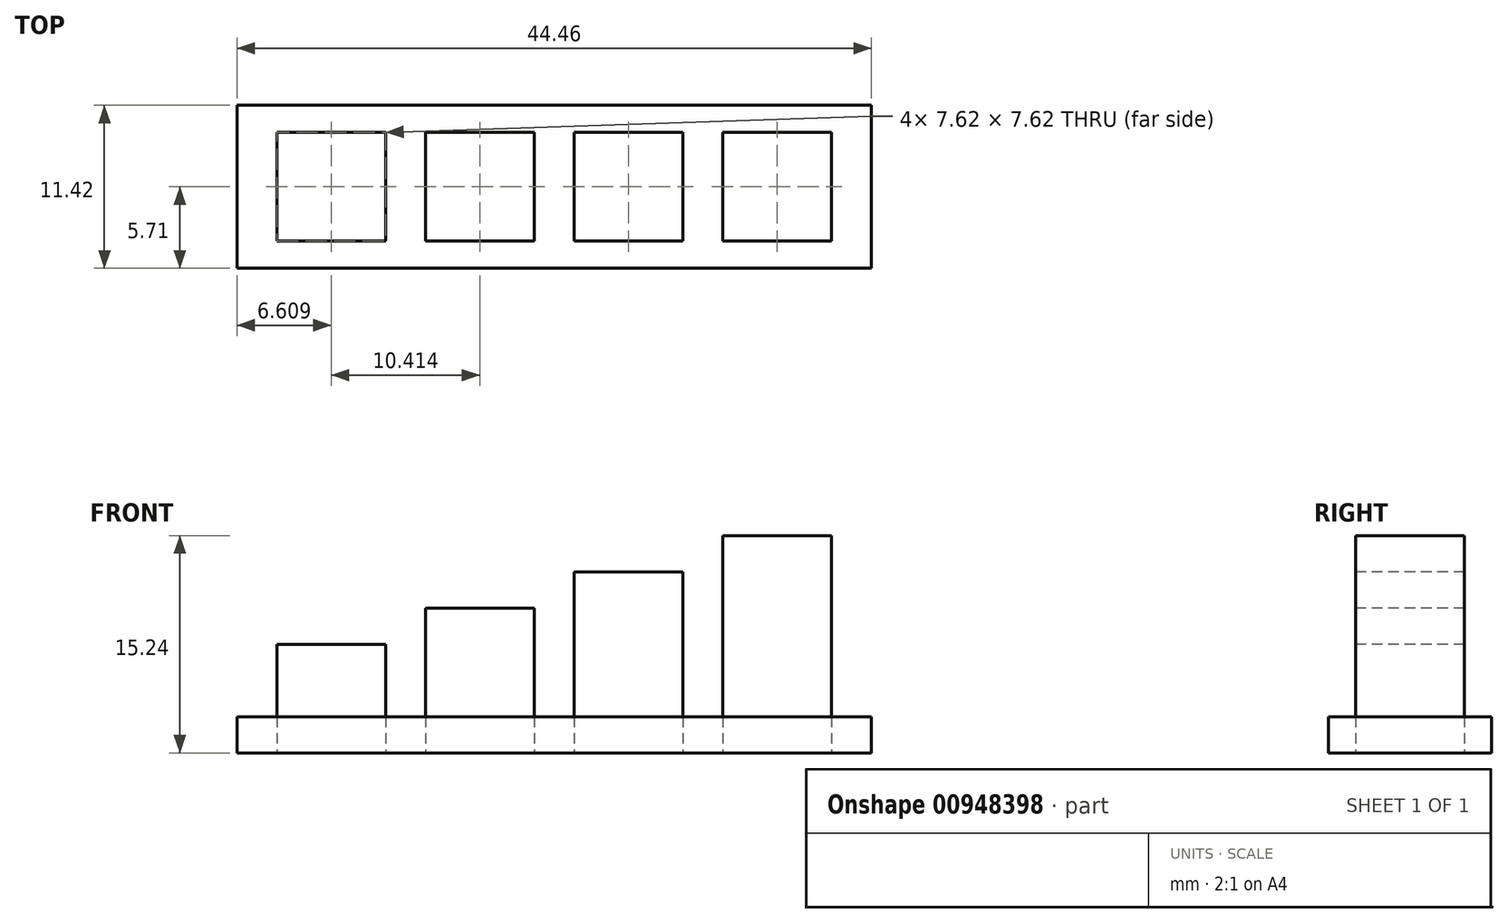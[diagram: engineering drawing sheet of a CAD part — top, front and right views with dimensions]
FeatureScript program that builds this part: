
annotation { "Feature Type Name" : "Feature", "Feature Type Description" : "" }
export const myFeature = defineFeature(function(context is Context, id is Id, definition is map)
    precondition{}
    {
        {
            var Q0;
            Q0=qCreatedBy(makeId("Top.planeOp"),FACE);
            var sketch = newSketch(context, id + "F0", { "sketchPlane" : qUnion([Q0])});
            skLineSegment(sketch, "E0.bottom", {"start": v(-22.23, 5.71) * mm, "end": v(22.22, 5.72) * mm});
            skLineSegment(sketch, "E0.top", {"start": v(-22.23, -5.72) * mm, "end": v(22.22, -5.71) * mm});
            skLineSegment(sketch, "E0.left", {"start": v(-22.23, 5.71) * mm, "end": v(-22.23, -5.72) * mm});
            skLineSegment(sketch, "E0.right", {"start": v(22.22, 5.72) * mm, "end": v(22.22, -5.72) * mm});
            skLineSegment(sketch, "E1.bottom", {"start": v(1.4, 3.81) * mm, "end": v(9.02, 3.81) * mm});
            skLineSegment(sketch, "E1.top", {"start": v(1.4, -3.81) * mm, "end": v(9.02, -3.81) * mm});
            skLineSegment(sketch, "E1.left", {"start": v(1.4, 3.81) * mm, "end": v(1.4, -3.81) * mm});
            skLineSegment(sketch, "E1.right", {"start": v(9.02, 3.81) * mm, "end": v(9.02, -3.81) * mm});
            skLineSegment(sketch, "E2.bottom", {"start": v(11.81, 3.81) * mm, "end": v(19.43, 3.81) * mm});
            skLineSegment(sketch, "E2.top", {"start": v(11.81, -3.81) * mm, "end": v(19.43, -3.81) * mm});
            skLineSegment(sketch, "E2.left", {"start": v(11.81, 3.81) * mm, "end": v(11.81, -3.81) * mm});
            skLineSegment(sketch, "E2.right", {"start": v(19.43, 3.81) * mm, "end": v(19.43, -3.81) * mm});
            skPoint(sketch, "E3", {"position": v(22.22, 0) * mm});
            skPoint(sketch, "E4", {"position": v(0, 0) * mm});
            skPoint(sketch, "E5", {"position": v(-22.23, 0) * mm});
            skPoint(sketch, "E6", {"position": v(11.81, 0) * mm});
            skPoint(sketch, "E7", {"position": v(19.43, 0) * mm});
            skPoint(sketch, "E8", {"position": v(9.02, 0) * mm});
            skPoint(sketch, "E9", {"position": v(1.4, 0) * mm});
            skLineSegment(sketch, "E10.bottom", {"start": v(-9.02, 3.8) * mm, "end": v(-1.4, 3.8) * mm});
            skLineSegment(sketch, "E10.top", {"start": v(-9.02, -3.8) * mm, "end": v(-1.4, -3.8) * mm});
            skLineSegment(sketch, "E10.left", {"start": v(-9.02, 3.8) * mm, "end": v(-9.02, -3.8) * mm});
            skLineSegment(sketch, "E10.right", {"start": v(-1.4, 3.81) * mm, "end": v(-1.4, -3.81) * mm});
            skPoint(sketch, "E11", {"position": v(-1.4, 0) * mm});
            skPoint(sketch, "E12", {"position": v(-9.02, 0) * mm});
            skLineSegment(sketch, "E13.bottom", {"start": v(-19.43, 3.8) * mm, "end": v(-11.81, 3.8) * mm});
            skLineSegment(sketch, "E13.top", {"start": v(-19.43, -3.81) * mm, "end": v(-11.81, -3.81) * mm});
            skLineSegment(sketch, "E13.left", {"start": v(-19.43, 3.8) * mm, "end": v(-19.43, -3.8) * mm});
            skLineSegment(sketch, "E13.right", {"start": v(-11.81, 3.8) * mm, "end": v(-11.81, -3.8) * mm});
            skPoint(sketch, "E14", {"position": v(-11.81, 0) * mm});
            skPoint(sketch, "E15", {"position": v(-19.43, 0) * mm});
            skSolve(sketch);
        }
        {
            var Q0;
            Q0=makeQuery(id+"F0.imprint","IMPRINT",FACE,{"disambiguationData":[TD([[makeQuery(id+"F0.imprint","IMPRINT",EDGE,{"derivedFrom":sQuery(id+"F0.wireOp",EDGE,"E10.bottom")}),-1.0]])]});
            var Q1;
            Q1=makeQuery(id+"F0.imprint","IMPRINT",FACE,{"disambiguationData":[TD([[makeQuery(id+"F0.imprint","IMPRINT",EDGE,{"derivedFrom":sQuery(id+"F0.wireOp",EDGE,"E13.bottom")}),-1.0]])]});
            var Q2;
            Q2=makeQuery(id+"F0.imprint","IMPRINT",FACE,{"disambiguationData":[TD([[makeQuery(id+"F0.imprint","IMPRINT",EDGE,{"derivedFrom":sQuery(id+"F0.wireOp",EDGE,"E1.bottom")}),-1.0]])]});
            var Q3;
            Q3=makeQuery(id+"F0.imprint","IMPRINT",FACE,{"disambiguationData":[TD([[makeQuery(id+"F0.imprint","IMPRINT",EDGE,{"derivedFrom":sQuery(id+"F0.wireOp",EDGE,"E2.bottom")}),-1.0]])]});
            extrude(context, id + "F1", {"entities" : qUnion([Q0, Q1, Q2, Q3]), "depth" : 7.62 * mm, "offsetDistance" : 25.4 * mm});
        }
        {
            var Q0;
            Q0=makeQuery(id+"F1.opExtrude","CAP_FACE",FACE,{"disambiguationData":[OSD([sQuery(id+"F0.wireOp",EDGE,"E10.bottom"),sQuery(id+"F0.wireOp",EDGE,"E10.top"),sQuery(id+"F0.wireOp",EDGE,"E10.left"),sQuery(id+"F0.wireOp",EDGE,"E10.right")])],"isStart":false});
            extrude(context, id + "F2", {"entities" : qUnion([Q0]), "operationType" : NewBodyOperationType.ADD, "depth" : 2.54 * mm, "offsetDistance" : 25.4 * mm});
        }
        {
            var Q0;
            Q0=makeQuery(id+"F1.opExtrude","CAP_FACE",FACE,{"disambiguationData":[OSD([sQuery(id+"F0.wireOp",EDGE,"E1.bottom"),sQuery(id+"F0.wireOp",EDGE,"E1.top"),sQuery(id+"F0.wireOp",EDGE,"E1.left"),sQuery(id+"F0.wireOp",EDGE,"E1.right")])],"isStart":false});
            extrude(context, id + "F3", {"entities" : qUnion([Q0]), "operationType" : NewBodyOperationType.ADD, "depth" : 5.08 * mm, "offsetDistance" : 25.4 * mm});
        }
        {
            var Q0;
            Q0=makeQuery(id+"F1.opExtrude","CAP_FACE",FACE,{"disambiguationData":[OSD([sQuery(id+"F0.wireOp",EDGE,"E2.bottom"),sQuery(id+"F0.wireOp",EDGE,"E2.top"),sQuery(id+"F0.wireOp",EDGE,"E2.left"),sQuery(id+"F0.wireOp",EDGE,"E2.right")])],"isStart":false});
            extrude(context, id + "F4", {"entities" : qUnion([Q0]), "operationType" : NewBodyOperationType.ADD, "depth" : 7.62 * mm, "offsetDistance" : 25.4 * mm});
        }
        {
            var Q0;
            Q0 = qSketchRegion(id + "F0", true);
            extrude(context, id + "F5", {"entities" : qUnion([Q0]), "depth" : 2.54 * mm, "offsetDistance" : 25.4 * mm});
        }
    });
